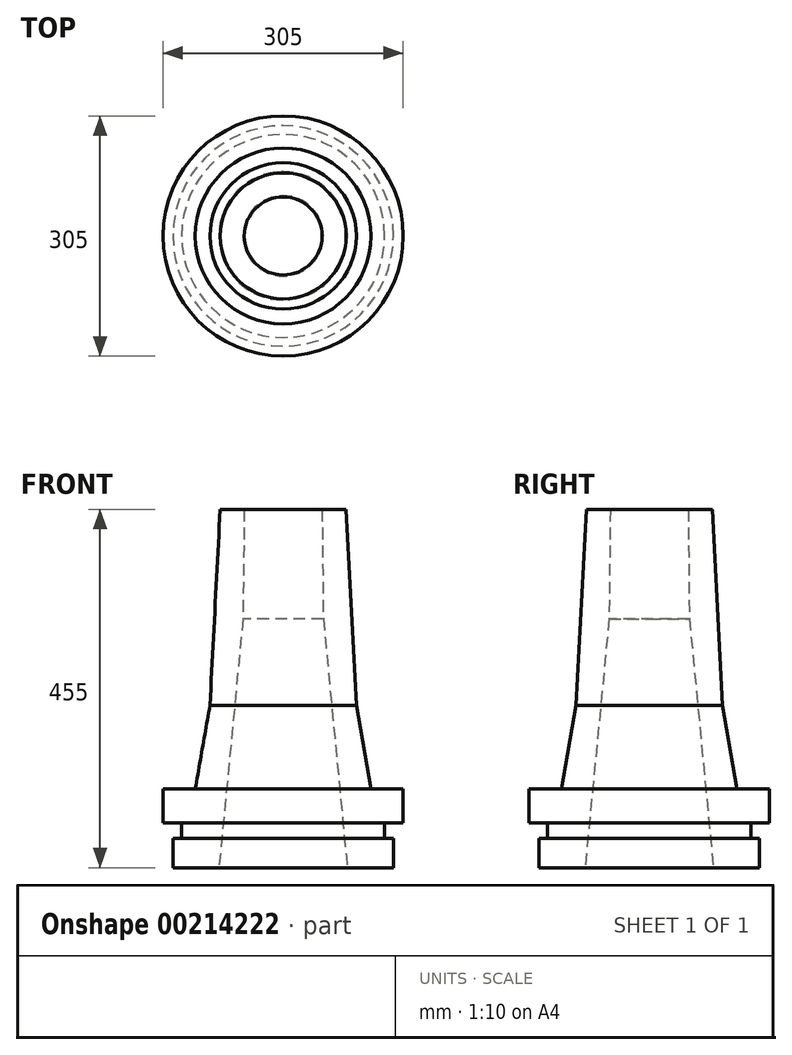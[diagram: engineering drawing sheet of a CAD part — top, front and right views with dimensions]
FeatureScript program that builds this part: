
annotation { "Feature Type Name" : "Feature", "Feature Type Description" : "" }
export const myFeature = defineFeature(function(context is Context, id is Id, definition is map)
    precondition{}
    {
        {
            var Q0;
            Q0=qCreatedBy(makeId("Front.planeOp"),FACE);
            var sketch = newSketch(context, id + "F0", { "sketchPlane" : qUnion([Q0])});
            skLineSegment(sketch, "E0", {"start": v(0, 0) * mm, "end": v(0, 89.01) * mm, "construction": true});
            skLineSegment(sketch, "E1", {"start": v(0, 455) * mm, "end": v(80, 455) * mm});
            skLineSegment(sketch, "E2", {"start": v(93, 206) * mm, "end": v(80, 455) * mm});
            skLineSegment(sketch, "E3", {"start": v(93, 206) * mm, "end": v(111.65, 100) * mm});
            skLineSegment(sketch, "E4", {"start": v(111.65, 100) * mm, "end": v(152.5, 100) * mm});
            skLineSegment(sketch, "E5", {"start": v(152.5, 100) * mm, "end": v(152.5, 57) * mm});
            skLineSegment(sketch, "E6", {"start": v(152.5, 57) * mm, "end": v(129, 57) * mm});
            skLineSegment(sketch, "E7", {"start": v(129, 57) * mm, "end": v(129, 37) * mm});
            skLineSegment(sketch, "E8", {"start": v(129, 37) * mm, "end": v(140, 37) * mm});
            skLineSegment(sketch, "E9", {"start": v(140, 37) * mm, "end": v(140, 0) * mm});
            skLineSegment(sketch, "E10", {"start": v(140, 0) * mm, "end": v(0, 0) * mm});
            skLineSegment(sketch, "E11", {"start": v(0, 0) * mm, "end": v(0, 455) * mm});
            skSolve(sketch);
        }
        {
            var Q0;
            Q0=makeQuery(id+"F0.imprint","IMPRINT",FACE,{"disambiguationData":[TD([[makeQuery(id+"F0.imprint","IMPRINT",EDGE,{"derivedFrom":sQuery(id+"F0.wireOp",EDGE,"E1")}),-1.0]])]});
            var Q1;
            Q1=sQuery(id+"F0.wireOp",EDGE,"E0");
            revolve(context, id + "F1", {"entities" : qUnion([Q0]), "axis" : qUnion([Q1]), "revolveType" : RevolveType.FULL});
        }
        {
            var Q0;
            Q0=qCreatedBy(makeId("Front.planeOp"),FACE);
            var sketch = newSketch(context, id + "F2", { "sketchPlane" : qUnion([Q0])});
            skLineSegment(sketch, "E12", {"start": v(0, 455) * mm, "end": v(49.5, 455) * mm});
            skLineSegment(sketch, "E13", {"start": v(49.5, 455) * mm, "end": v(51, 316) * mm});
            skLineSegment(sketch, "E14", {"start": v(51, 316) * mm, "end": v(81.5, 0) * mm});
            skLineSegment(sketch, "E15", {"start": v(81.5, 0) * mm, "end": v(0, 0) * mm});
            skLineSegment(sketch, "E16", {"start": v(0, 0) * mm, "end": v(0, 455) * mm});
            skSolve(sketch);
        }
        {
            var Q0;
            Q0=makeQuery(id+"F2.imprint","IMPRINT",FACE,{"disambiguationData":[TD([[makeQuery(id+"F2.imprint","IMPRINT",EDGE,{"derivedFrom":sQuery(id+"F2.wireOp",EDGE,"E12")}),-1.0]])]});
            var Q1;
            Q1=sQuery(id+"F2.wireOp",EDGE,"E16");
            revolve(context, id + "F3", {"operationType" : NewBodyOperationType.REMOVE, "entities" : qUnion([Q0]), "axis" : qUnion([Q1]), "revolveType" : RevolveType.FULL, "oppositeDirection" : true});
        }
    });
